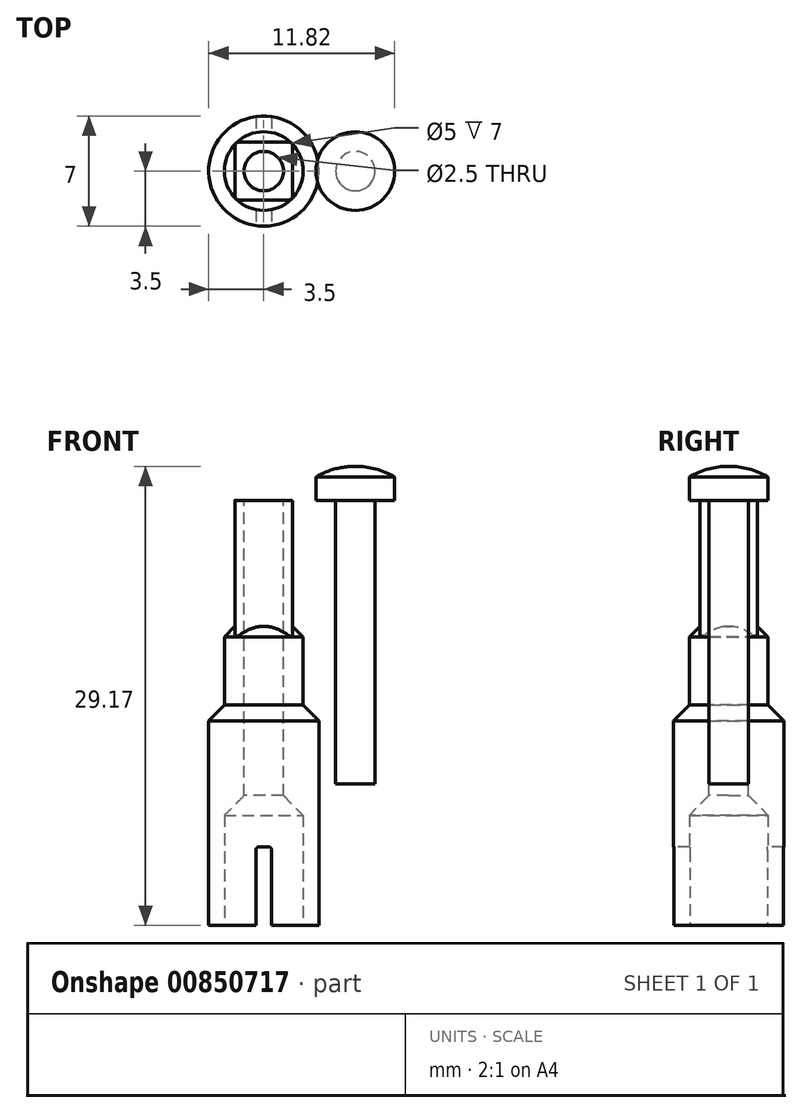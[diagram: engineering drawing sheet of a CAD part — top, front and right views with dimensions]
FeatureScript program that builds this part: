
annotation { "Feature Type Name" : "Feature", "Feature Type Description" : "" }
export const myFeature = defineFeature(function(context is Context, id is Id, definition is map)
    precondition{}
    {
        {
            var Q0;
            Q0=qCreatedBy(makeId("Top.planeOp"),FACE);
            var sketch = newSketch(context, id + "F0", { "sketchPlane" : qUnion([Q0])});
            skCircle(sketch, "E0", {"center": v(0, 0) * mm, "radius": 3.5 * mm});
            skSolve(sketch);
        }
        {
            var Q0;
            Q0 = qSketchRegion(id + "F0", true);
            extrude(context, id + "F1", {"entities" : qUnion([Q0]), "depth" : 14 * mm, "offsetDistance" : 25 * mm});
        }
        {
            var Q0;
            Q0=makeQuery(id+"F1.opExtrude","CAP_FACE",FACE,{"disambiguationData":[OSD([sQuery(id+"F0.wireOp",EDGE,"E0")])],"isStart":false});
            var sketch = newSketch(context, id + "F2", { "sketchPlane" : qUnion([Q0])});
            skCircle(sketch, "E1", {"center": v(0, 0) * mm, "radius": 2.5 * mm});
            skSolve(sketch);
        }
        {
            var Q0;
            Q0 = qSketchRegion(id + "F2", true);
            extrude(context, id + "F3", {"entities" : qUnion([Q0]), "operationType" : NewBodyOperationType.ADD, "depth" : 5 * mm, "offsetDistance" : 25 * mm});
        }
        {
            var Q0;
            Q0=makeQuery(id+"F3.opExtrude","CAP_FACE",FACE,{"disambiguationData":[OSD([sQuery(id+"F2.wireOp",EDGE,"E1")])],"isStart":false});
            var sketch = newSketch(context, id + "F4", { "sketchPlane" : qUnion([Q0])});
            skLineSegment(sketch, "E2.bottom", {"start": v(1.63, 1.83) * mm, "end": v(-1.63, 1.83) * mm});
            skLineSegment(sketch, "E2.top", {"start": v(1.63, -1.83) * mm, "end": v(-1.63, -1.83) * mm});
            skLineSegment(sketch, "E2.left", {"start": v(1.83, 1.63) * mm, "end": v(1.83, -1.63) * mm});
            skLineSegment(sketch, "E2.right", {"start": v(-1.83, 1.63) * mm, "end": v(-1.83, -1.63) * mm});
            skPoint(sketch, "E2.middle", {"position": v(0, 0) * mm});
            skPoint(sketch, "E3.visualSharp", {"position": v(-1.83, 1.83) * mm});
            skArc(sketch, "E3.filletArc", {"start": v(-1.63, 1.83) * mm, "mid": v(-1.77, 1.77) * mm, "end": v(-1.83, 1.63) * mm});
            skPoint(sketch, "E4.visualSharp", {"position": v(1.83, 1.83) * mm});
            skArc(sketch, "E4.filletArc", {"start": v(1.83, 1.63) * mm, "mid": v(1.77, 1.77) * mm, "end": v(1.63, 1.83) * mm});
            skPoint(sketch, "E5.visualSharp", {"position": v(1.83, -1.83) * mm});
            skArc(sketch, "E5.filletArc", {"start": v(1.63, -1.83) * mm, "mid": v(1.77, -1.77) * mm, "end": v(1.83, -1.63) * mm});
            skPoint(sketch, "E6.visualSharp", {"position": v(-1.83, -1.83) * mm});
            skArc(sketch, "E6.filletArc", {"start": v(-1.83, -1.63) * mm, "mid": v(-1.77, -1.77) * mm, "end": v(-1.63, -1.83) * mm});
            skSolve(sketch);
        }
        {
            var Q0;
            Q0 = qSketchRegion(id + "F4", true);
            extrude(context, id + "F5", {"entities" : qUnion([Q0]), "operationType" : NewBodyOperationType.ADD, "depth" : 8 * mm, "offsetDistance" : 25 * mm});
        }
        {
            var Q0;
            Q0=makeQuery(id+"F1.opExtrude","CAP_FACE",FACE,{"disambiguationData":[OSD([sQuery(id+"F0.wireOp",EDGE,"E0")])],"isStart":true});
            var sketch = newSketch(context, id + "F6", { "sketchPlane" : qUnion([Q0])});
            skCircle(sketch, "E7", {"center": v(0, 0) * mm, "radius": 2.5 * mm});
            skSolve(sketch);
        }
        {
            var Q0;
            Q0 = qSketchRegion(id + "F6", true);
            extrude(context, id + "F7", {"entities" : qUnion([Q0]), "operationType" : NewBodyOperationType.REMOVE, "oppositeDirection" : true, "depth" : 7 * mm, "offsetDistance" : 25 * mm});
        }
        {
            var Q0;
            Q0=qCreatedBy(makeId("Front.planeOp"),FACE);
            var sketch = newSketch(context, id + "F8", { "sketchPlane" : qUnion([Q0])});
            skLineSegment(sketch, "E8.bottom", {"start": v(-0.5, 0) * mm, "end": v(0.5, 0) * mm});
            skLineSegment(sketch, "E8.top", {"start": v(-0.3, 5) * mm, "end": v(0.3, 5) * mm});
            skLineSegment(sketch, "E8.left", {"start": v(-0.5, 0) * mm, "end": v(-0.5, 4.8) * mm});
            skLineSegment(sketch, "E8.right", {"start": v(0.5, 0) * mm, "end": v(0.5, 4.8) * mm});
            skPoint(sketch, "E9.visualSharp", {"position": v(-0.5, 5) * mm});
            skArc(sketch, "E9.filletArc", {"start": v(-0.3, 5) * mm, "mid": v(-0.44, 4.94) * mm, "end": v(-0.5, 4.8) * mm});
            skPoint(sketch, "E10.visualSharp", {"position": v(0.5, 5) * mm});
            skArc(sketch, "E10.filletArc", {"start": v(0.5, 4.8) * mm, "mid": v(0.44, 4.94) * mm, "end": v(0.3, 5) * mm});
            skSolve(sketch);
        }
        {
            var Q0;
            Q0 = qSketchRegion(id + "F8", true);
            var Q1;
            Q1=makeQuery(id+"F1.opExtrude","SWEPT_FACE",FACE,{"disambiguationData":[OSD([sQuery(id+"F0.wireOp",EDGE,"E0")])]});
            var Q2;
            Q2=makeQuery(id+"F1.opExtrude","SWEPT_FACE",FACE,{"disambiguationData":[OSD([sQuery(id+"F0.wireOp",EDGE,"E0")])]});
            extrude(context, id + "F9", {"entities" : qUnion([Q0]), "operationType" : NewBodyOperationType.REMOVE, "endBound" : BoundingType.UP_TO_SURFACE, "oppositeDirection" : true, "depth" : 25 * mm, "endBoundEntityFace" : qUnion([Q1]), "offsetDistance" : 25 * mm, "hasSecondDirection" : true, "secondDirectionBound" : BoundingType.UP_TO_SURFACE, "secondDirectionOppositeDirection" : false, "secondDirectionDepth" : 25 * mm, "secondDirectionBoundEntityFace" : qUnion([Q2])});
        }
        {
            var Q0;
            Q0=makeQuery(id+"F1.opExtrude","CAP_EDGE",EDGE,{"disambiguationData":[OSD([sQuery(id+"F0.wireOp",EDGE,"E0")])],"isStart":false});
            chamfer(context, id + "F10", {"entities" : qUnion([Q0]), "width" : 1 * mm, "tangentPropagation" : true});
        }
        {
            var Q0;
            {var subQ0=sQuery(id+"F2.wireOp",EDGE,"E1");Q0=makeQuery(id+"F5.boolean.opBoolean","SPLIT",EDGE,{"disambiguationData":[TD([makeQuery(id+"F3.opExtrude","SWEPT_FACE",FACE,{"disambiguationData":[OSD([subQ0])]}),makeQuery(id+"F3.opExtrude","CAP_FACE",FACE,{"disambiguationData":[OSD([subQ0])],"isStart":false}),makeQuery(id+"F5.opExtrude","SWEPT_FACE",FACE,{"disambiguationData":[OSD([sQuery(id+"F4.wireOp",EDGE,"E5.filletArc")])]}),makeQuery(id+"F5.opExtrude","SWEPT_FACE",FACE,{"disambiguationData":[OSD([sQuery(id+"F4.wireOp",EDGE,"E6.filletArc")])]})])],"derivedFrom":makeQuery(id+"F3.opExtrude","CAP_EDGE",EDGE,{"disambiguationData":[OSD([subQ0])],"isStart":false})});}
            chamfer(context, id + "F11", {"entities" : qUnion([Q0]), "width" : 0.66 * mm, "tangentPropagation" : true});
        }
        {
            var Q0;
            Q0=makeQuery(id+"F5.opExtrude","CAP_FACE",FACE,{"disambiguationData":[OSD([sQuery(id+"F4.wireOp",EDGE,"E2.bottom"),sQuery(id+"F4.wireOp",EDGE,"E2.top"),sQuery(id+"F4.wireOp",EDGE,"E2.left"),sQuery(id+"F4.wireOp",EDGE,"E2.right"),sQuery(id+"F4.wireOp",EDGE,"E3.filletArc"),sQuery(id+"F4.wireOp",EDGE,"E4.filletArc"),sQuery(id+"F4.wireOp",EDGE,"E5.filletArc"),sQuery(id+"F4.wireOp",EDGE,"E6.filletArc")])],"isStart":false});
            var sketch = newSketch(context, id + "F12", { "sketchPlane" : qUnion([Q0])});
            skCircle(sketch, "E11", {"center": v(0, 0) * mm, "radius": 1.25 * mm});
            skSolve(sketch);
        }
        {
            var Q0;
            Q0 = qSketchRegion(id + "F12", true);
            extrude(context, id + "F13", {"entities" : qUnion([Q0]), "operationType" : NewBodyOperationType.REMOVE, "endBound" : BoundingType.THROUGH_ALL, "oppositeDirection" : true, "depth" : 25 * mm, "offsetDistance" : 25 * mm});
        }
        {
            var Q0;
            Q0=makeQuery(id+"F13.boolean.opBoolean","INTERSECT",EDGE,{"derivedFrom":[makeQuery(id+"F7.boolean.opBoolean","COPY",FACE,{"derivedFrom":makeQuery(id+"F7.opExtrude","CAP_FACE",FACE,{"disambiguationData":[OSD([sQuery(id+"F6.wireOp",EDGE,"E7")])],"isStart":false})}),makeQuery(id+"F13.opExtrude","SWEPT_FACE",FACE,{"disambiguationData":[OSD([sQuery(id+"F12.wireOp",EDGE,"E11")])]})]});
            chamfer(context, id + "F14", {"entities" : qUnion([Q0]), "width" : 1.25 * mm, "tangentPropagation" : true});
        }
        {
            var Q0;
            Q0=qCreatedBy(makeId("Front.planeOp"),FACE);
            var sketch = newSketch(context, id + "F15", { "sketchPlane" : qUnion([Q0])});
            skLineSegment(sketch, "E12.bottom", {"start": v(4.57, 9) * mm, "end": v(5.82, 9) * mm});
            skLineSegment(sketch, "E12.left", {"start": v(4.57, 9) * mm, "end": v(4.57, 27) * mm});
            skLineSegment(sketch, "E12.right", {"start": v(5.82, 9) * mm, "end": v(5.82, 27) * mm});
            skLineSegment(sketch, "E13", {"start": v(4.57, 27) * mm, "end": v(3.32, 27) * mm});
            skLineSegment(sketch, "E14", {"start": v(3.32, 27) * mm, "end": v(3.32, 28.5) * mm});
            skLineSegment(sketch, "E15", {"start": v(5.82, 27) * mm, "end": v(5.82, 29.17) * mm});
            skArc(sketch, "E16", {"start": v(5.82, 29.17) * mm, "mid": v(4.52, 29) * mm, "end": v(3.32, 28.5) * mm});
            skLineSegment(sketch, "E17", {"start": v(4.57, 27) * mm, "end": v(5.82, 27) * mm, "construction": true});
            skSolve(sketch);
        }
        {
            var Q0;
            Q0 = qSketchRegion(id + "F15", true);
            var Q1;
            Q1=sQuery(id+"F15.wireOp",EDGE,"E12.right");
            revolve(context, id + "F16", {"surfaceOperationType" : NewSurfaceOperationType.NEW, "entities" : qUnion([Q0]), "axis" : qUnion([Q1]), "revolveType" : RevolveType.FULL});
        }
    });
